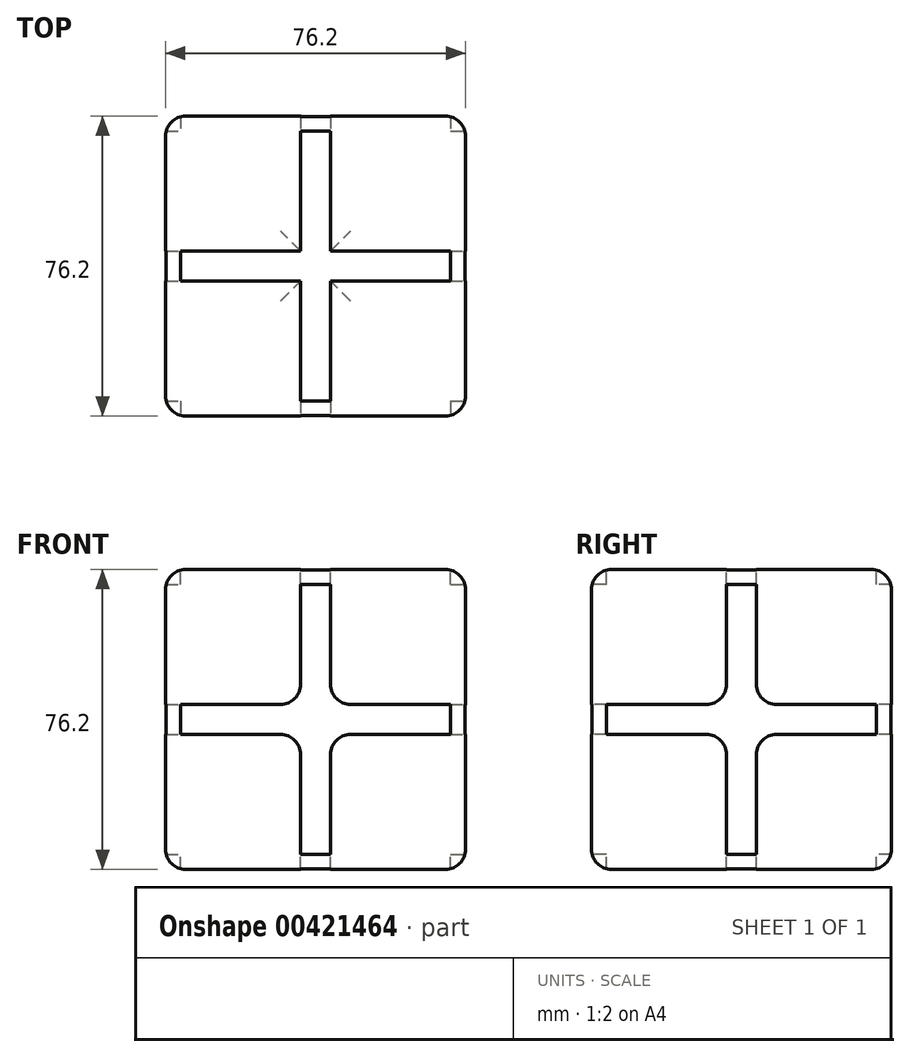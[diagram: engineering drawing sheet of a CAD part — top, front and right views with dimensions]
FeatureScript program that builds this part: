
annotation { "Feature Type Name" : "Feature", "Feature Type Description" : "" }
export const myFeature = defineFeature(function(context is Context, id is Id, definition is map)
    precondition{}
    {
        {
            var Q0;
            Q0=qCreatedBy(makeId("Top.planeOp"),FACE);
            var sketch = newSketch(context, id + "F0", { "sketchPlane" : qUnion([Q0])});
            skLineSegment(sketch, "E0.bottom", {"start": v(-38.1, 38.1) * mm, "end": v(38.1, 38.1) * mm});
            skLineSegment(sketch, "E0.top", {"start": v(-38.1, -38.1) * mm, "end": v(38.1, -38.1) * mm});
            skLineSegment(sketch, "E0.left", {"start": v(-38.1, 38.1) * mm, "end": v(-38.1, -38.1) * mm});
            skLineSegment(sketch, "E0.right", {"start": v(38.1, 38.1) * mm, "end": v(38.1, -38.1) * mm});
            skSolve(sketch);
        }
        {
            var Q0;
            Q0=makeQuery(id+"F0.imprint","IMPRINT",FACE,{"disambiguationData":[TD([[makeQuery(id+"F0.imprint","IMPRINT",EDGE,{"derivedFrom":sQuery(id+"F0.wireOp",EDGE,"E0.bottom")}),-1.0]])]});
            extrude(context, id + "F1", {"entities" : qUnion([Q0]), "depth" : 76.2 * mm});
        }
        {
            var Q0;
            Q0=makeQuery(id+"F1.opExtrude","SWEPT_FACE",FACE,{"disambiguationData":[OSD([sQuery(id+"F0.wireOp",EDGE,"E0.top")])]});
            var sketch = newSketch(context, id + "F2", { "sketchPlane" : qUnion([Q0])});
            skLineSegment(sketch, "E1", {"start": v(-34.3, 41.91) * mm, "end": v(-3.81, 41.91) * mm});
            skLineSegment(sketch, "E2", {"start": v(-34.3, 34.3) * mm, "end": v(-3.81, 34.3) * mm});
            skLineSegment(sketch, "E3", {"start": v(-3.81, 41.91) * mm, "end": v(-3.81, 72.39) * mm});
            skLineSegment(sketch, "E4", {"start": v(-3.81, 34.3) * mm, "end": v(-3.81, 3.8) * mm});
            skLineSegment(sketch, "E5", {"start": v(34.3, 41.91) * mm, "end": v(3.8, 41.91) * mm});
            skLineSegment(sketch, "E6", {"start": v(34.3, 34.3) * mm, "end": v(3.8, 34.3) * mm});
            skLineSegment(sketch, "E7", {"start": v(3.8, 41.91) * mm, "end": v(3.8, 72.39) * mm});
            skLineSegment(sketch, "E8", {"start": v(3.8, 34.3) * mm, "end": v(3.8, 3.81) * mm});
            skLineSegment(sketch, "E9", {"start": v(-34.3, 41.9) * mm, "end": v(-34.3, 34.3) * mm});
            skLineSegment(sketch, "E10.MirrorCS", {"start": v(34.3, 41.9) * mm, "end": v(34.3, 34.3) * mm});
            skPoint(sketch, "E11.right.end.orphan", {"position": v(38.1, 34.3) * mm});
            skPoint(sketch, "E11.right.start.orphan", {"position": v(38.1, 41.91) * mm});
            skLineSegment(sketch, "E12", {"start": v(-3.81, 3.8) * mm, "end": v(3.8, 3.8) * mm});
            skLineSegment(sketch, "E13.MirrorCS", {"start": v(-3.81, 72.39) * mm, "end": v(3.8, 72.39) * mm});
            skPoint(sketch, "E14.end.orphan", {"position": v(34.3, 38.1) * mm});
            skPoint(sketch, "E14.start.orphan", {"position": v(-34.3, 38.1) * mm});
            skSolve(sketch);
        }
        {
            var Q0;
            Q0=makeQuery(id+"F2.imprint","IMPRINT",FACE,{"disambiguationData":[TD([[makeQuery(id+"F2.imprint","IMPRINT",EDGE,{"derivedFrom":sQuery(id+"F2.wireOp",EDGE,"E1")}),-1.0]])]});
            extrude(context, id + "F3", {"entities" : qUnion([Q0]), "operationType" : NewBodyOperationType.REMOVE, "oppositeDirection" : true, "depth" : 76.2 * mm});
        }
        {
            var Q0;
            Q0=makeQuery(id+"F1.opExtrude","CAP_FACE",FACE,{"disambiguationData":[OSD([sQuery(id+"F0.wireOp",EDGE,"E0.bottom"),sQuery(id+"F0.wireOp",EDGE,"E0.top"),sQuery(id+"F0.wireOp",EDGE,"E0.left"),sQuery(id+"F0.wireOp",EDGE,"E0.right")])],"isStart":false});
            var sketch = newSketch(context, id + "F4", { "sketchPlane" : qUnion([Q0])});
            skLineSegment(sketch, "E15", {"start": v(-3.81, 34.3) * mm, "end": v(-3.81, 3.8) * mm});
            skPoint(sketch, "E15.endSnap0", {"position": v(0, -38.1) * mm});
            skLineSegment(sketch, "E16", {"start": v(3.8, -34.29) * mm, "end": v(3.8, -3.8) * mm});
            skLineSegment(sketch, "E17", {"start": v(-34.3, 3.8) * mm, "end": v(-3.81, 3.8) * mm});
            skLineSegment(sketch, "E18", {"start": v(34.29, -3.8) * mm, "end": v(3.8, -3.8) * mm});
            skLineSegment(sketch, "E19.trimOffspring", {"start": v(3.8, 3.8) * mm, "end": v(34.29, 3.8) * mm});
            skLineSegment(sketch, "E20.trimOffspring", {"start": v(-3.81, -3.81) * mm, "end": v(-3.81, -34.29) * mm});
            skLineSegment(sketch, "E21.trimOffspring", {"start": v(3.8, 3.8) * mm, "end": v(3.8, 34.3) * mm});
            skLineSegment(sketch, "E22.trimOffspring", {"start": v(-3.81, -3.8) * mm, "end": v(-34.3, -3.81) * mm});
            skLineSegment(sketch, "E23", {"start": v(-34.3, 3.8) * mm, "end": v(-34.3, -3.81) * mm});
            skLineSegment(sketch, "E24", {"start": v(34.29, 3.8) * mm, "end": v(34.29, -3.8) * mm});
            skLineSegment(sketch, "E25", {"start": v(-3.81, 34.3) * mm, "end": v(3.8, 34.3) * mm});
            skLineSegment(sketch, "E26", {"start": v(-3.81, -34.29) * mm, "end": v(3.8, -34.29) * mm});
            skPoint(sketch, "E27.start.orphan", {"position": v(-3.81, -38.1) * mm});
            skSolve(sketch);
        }
        {
            var Q0;
            Q0=makeQuery(id+"F4.imprint","IMPRINT",FACE,{"disambiguationData":[TD([[makeQuery(id+"F4.imprint","IMPRINT",EDGE,{"derivedFrom":sQuery(id+"F4.wireOp",EDGE,"E15")}),1.0]])]});
            extrude(context, id + "F5", {"entities" : qUnion([Q0]), "operationType" : NewBodyOperationType.REMOVE, "oppositeDirection" : true, "depth" : 76.2 * mm});
        }
        {
            var Q0;
            Q0=makeQuery(id+"F1.opExtrude","SWEPT_FACE",FACE,{"disambiguationData":[OSD([sQuery(id+"F0.wireOp",EDGE,"E0.right")])]});
            var sketch = newSketch(context, id + "F6", { "sketchPlane" : qUnion([Q0])});
            skLineSegment(sketch, "E28", {"start": v(-34.3, 41.9) * mm, "end": v(-3.8, 41.9) * mm});
            skLineSegment(sketch, "E29", {"start": v(34.29, 34.3) * mm, "end": v(3.8, 34.3) * mm});
            skLineSegment(sketch, "E30", {"start": v(-3.8, 72.4) * mm, "end": v(-3.8, 41.9) * mm});
            skLineSegment(sketch, "E31", {"start": v(3.8, 3.81) * mm, "end": v(3.8, 34.3) * mm});
            skLineSegment(sketch, "E32", {"start": v(3.8, 72.4) * mm, "end": v(-3.8, 72.4) * mm});
            skLineSegment(sketch, "E33.trimOffspring", {"start": v(-3.8, 34.3) * mm, "end": v(-3.8, 3.81) * mm});
            skLineSegment(sketch, "E34.trimOffspring", {"start": v(3.8, 41.9) * mm, "end": v(34.29, 41.91) * mm});
            skLineSegment(sketch, "E35.trimOffspring", {"start": v(3.8, 41.9) * mm, "end": v(3.8, 72.4) * mm});
            skLineSegment(sketch, "E36.trimOffspring", {"start": v(-3.8, 34.3) * mm, "end": v(-34.3, 34.3) * mm});
            skLineSegment(sketch, "E37", {"start": v(-3.8, 3.81) * mm, "end": v(3.8, 3.81) * mm});
            skLineSegment(sketch, "E38", {"start": v(-34.3, 41.9) * mm, "end": v(-34.3, 34.3) * mm});
            skPoint(sketch, "E39.end.orphan", {"position": v(-41.91, 41.9) * mm});
            skPoint(sketch, "E40.orphan", {"position": v(-41.91, 34.3) * mm});
            skLineSegment(sketch, "E41.MirrorCS", {"start": v(34.29, 41.9) * mm, "end": v(34.29, 34.3) * mm});
            skSolve(sketch);
        }
        {
            var Q0;
            Q0=makeQuery(id+"F6.imprint","IMPRINT",FACE,{"disambiguationData":[TD([[makeQuery(id+"F6.imprint","IMPRINT",EDGE,{"derivedFrom":sQuery(id+"F6.wireOp",EDGE,"E28")}),-1.0]])]});
            extrude(context, id + "F7", {"entities" : qUnion([Q0]), "operationType" : NewBodyOperationType.REMOVE, "oppositeDirection" : true, "depth" : 76.2 * mm});
        }
        {
            var Q0;
            Q0=makeQuery(id+"F1.opExtrude","SWEPT_EDGE",EDGE,{"disambiguationData":[OSD([sQuery(id+"F0.wireOp",EDGE,"E0.top"),sQuery(id+"F0.wireOp",EDGE,"E0.right")])]});
            var Q1;
            Q1=makeQuery(id+"F1.opExtrude","CAP_EDGE",EDGE,{"disambiguationData":[OSD([sQuery(id+"F0.wireOp",EDGE,"E0.top")])],"isStart":false});
            var Q2;
            Q2=makeQuery(id+"F1.opExtrude","CAP_EDGE",EDGE,{"disambiguationData":[OSD([sQuery(id+"F0.wireOp",EDGE,"E0.right")])],"isStart":false});
            var Q3;
            Q3=makeQuery(id+"F1.opExtrude","SWEPT_EDGE",EDGE,{"disambiguationData":[OSD([sQuery(id+"F0.wireOp",EDGE,"E0.top"),sQuery(id+"F0.wireOp",EDGE,"E0.left")])]});
            var Q4;
            Q4=makeQuery(id+"F1.opExtrude","CAP_EDGE",EDGE,{"disambiguationData":[OSD([sQuery(id+"F0.wireOp",EDGE,"E0.top")])],"isStart":true});
            var Q5;
            Q5=makeQuery(id+"F1.opExtrude","CAP_EDGE",EDGE,{"disambiguationData":[OSD([sQuery(id+"F0.wireOp",EDGE,"E0.right")])],"isStart":true});
            var Q6;
            Q6=makeQuery(id+"F1.opExtrude","SWEPT_EDGE",EDGE,{"disambiguationData":[OSD([sQuery(id+"F0.wireOp",EDGE,"E0.bottom"),sQuery(id+"F0.wireOp",EDGE,"E0.right")])]});
            var Q7;
            Q7=makeQuery(id+"F1.opExtrude","CAP_EDGE",EDGE,{"disambiguationData":[OSD([sQuery(id+"F0.wireOp",EDGE,"E0.bottom")])],"isStart":false});
            var Q8;
            Q8=makeQuery(id+"F1.opExtrude","CAP_EDGE",EDGE,{"disambiguationData":[OSD([sQuery(id+"F0.wireOp",EDGE,"E0.left")])],"isStart":false});
            var Q9;
            Q9=makeQuery(id+"F1.opExtrude","SWEPT_EDGE",EDGE,{"disambiguationData":[OSD([sQuery(id+"F0.wireOp",EDGE,"E0.bottom"),sQuery(id+"F0.wireOp",EDGE,"E0.left")])]});
            var Q10;
            Q10=makeQuery(id+"F1.opExtrude","CAP_EDGE",EDGE,{"disambiguationData":[OSD([sQuery(id+"F0.wireOp",EDGE,"E0.left")])],"isStart":true});
            var Q11;
            Q11=makeQuery(id+"F1.opExtrude","CAP_EDGE",EDGE,{"disambiguationData":[OSD([sQuery(id+"F0.wireOp",EDGE,"E0.bottom")])],"isStart":true});
            fillet(context, id + "F8", {"entities" : qUnion([Q0, Q1, Q2, Q3, Q4, Q5, Q6, Q7, Q8, Q9, Q10, Q11]), "radius" : 5.08 * mm, "tangentPropagation" : true, "allowEdgeOverflow" : false});
        }
        {
            var Q0;
            {var subQ0=sQuery(id+"F2.wireOp",EDGE,"E6");var subQ1=sQuery(id+"F2.wireOp",EDGE,"E8");Q0=makeQuery(id+"F5.boolean.opBoolean","SPLIT",EDGE,{"disambiguationData":[topologyDisambiguationEdgeConnected([makeQuery(id+"F5.opExtrude","SWEPT_FACE",FACE,{"disambiguationData":[OSD([sQuery(id+"F4.wireOp",EDGE,"E21.trimOffspring")])]})])],"derivedFrom":makeQuery(id+"F3.boolean.opBoolean","COPY",EDGE,{"derivedFrom":makeQuery(id+"F3.opExtrude","SWEPT_EDGE",EDGE,{"disambiguationData":[OSD([subQ0,subQ1])]})})});}
            var Q1;
            {var subQ0=sQuery(id+"F2.wireOp",EDGE,"E5");var subQ1=sQuery(id+"F2.wireOp",EDGE,"E7");Q1=makeQuery(id+"F5.boolean.opBoolean","SPLIT",EDGE,{"disambiguationData":[topologyDisambiguationEdgeConnected([makeQuery(id+"F5.opExtrude","SWEPT_FACE",FACE,{"disambiguationData":[OSD([sQuery(id+"F4.wireOp",EDGE,"E21.trimOffspring")])]})])],"derivedFrom":makeQuery(id+"F3.boolean.opBoolean","COPY",EDGE,{"derivedFrom":makeQuery(id+"F3.opExtrude","SWEPT_EDGE",EDGE,{"disambiguationData":[OSD([subQ0,subQ1])]})})});}
            var Q2;
            {var subQ0=sQuery(id+"F2.wireOp",EDGE,"E2");var subQ1=sQuery(id+"F2.wireOp",EDGE,"E4");Q2=makeQuery(id+"F5.boolean.opBoolean","SPLIT",EDGE,{"disambiguationData":[topologyDisambiguationEdgeConnected([makeQuery(id+"F5.opExtrude","SWEPT_FACE",FACE,{"disambiguationData":[OSD([sQuery(id+"F4.wireOp",EDGE,"E15")])]})])],"derivedFrom":makeQuery(id+"F3.boolean.opBoolean","COPY",EDGE,{"derivedFrom":makeQuery(id+"F3.opExtrude","SWEPT_EDGE",EDGE,{"disambiguationData":[OSD([subQ0,subQ1])]})})});}
            var Q3;
            {var subQ0=sQuery(id+"F2.wireOp",EDGE,"E1");var subQ1=sQuery(id+"F2.wireOp",EDGE,"E3");Q3=makeQuery(id+"F5.boolean.opBoolean","SPLIT",EDGE,{"disambiguationData":[topologyDisambiguationEdgeConnected([makeQuery(id+"F5.opExtrude","SWEPT_FACE",FACE,{"disambiguationData":[OSD([sQuery(id+"F4.wireOp",EDGE,"E15")])]})])],"derivedFrom":makeQuery(id+"F3.boolean.opBoolean","COPY",EDGE,{"derivedFrom":makeQuery(id+"F3.opExtrude","SWEPT_EDGE",EDGE,{"disambiguationData":[OSD([subQ0,subQ1])]})})});}
            var Q4;
            Q4=makeQuery(id+"F7.boolean.opBoolean","MERGE",EDGE,{"derivedFrom":[makeQuery(id+"F5.boolean.opBoolean","INTERSECT",EDGE,{"derivedFrom":[makeQuery(id+"F3.boolean.opBoolean","COPY",FACE,{"derivedFrom":makeQuery(id+"F3.opExtrude","SWEPT_FACE",FACE,{"disambiguationData":[OSD([sQuery(id+"F2.wireOp",EDGE,"E6")])]})}),makeQuery(id+"F5.opExtrude","SWEPT_FACE",FACE,{"disambiguationData":[OSD([sQuery(id+"F4.wireOp",EDGE,"E19.trimOffspring")])]})]}),makeQuery(id+"F7.opExtrude","SWEPT_EDGE",EDGE,{"disambiguationData":[OSD([sQuery(id+"F6.wireOp",EDGE,"E29"),sQuery(id+"F6.wireOp",EDGE,"E31")])]})]});
            var Q5;
            Q5=makeQuery(id+"F7.boolean.opBoolean","MERGE",EDGE,{"derivedFrom":[makeQuery(id+"F5.boolean.opBoolean","INTERSECT",EDGE,{"derivedFrom":[makeQuery(id+"F3.boolean.opBoolean","COPY",FACE,{"derivedFrom":makeQuery(id+"F3.opExtrude","SWEPT_FACE",FACE,{"disambiguationData":[OSD([sQuery(id+"F2.wireOp",EDGE,"E6")])]})}),makeQuery(id+"F5.opExtrude","SWEPT_FACE",FACE,{"disambiguationData":[OSD([sQuery(id+"F4.wireOp",EDGE,"E18")])]})]}),makeQuery(id+"F7.opExtrude","SWEPT_EDGE",EDGE,{"disambiguationData":[OSD([sQuery(id+"F6.wireOp",EDGE,"E33.trimOffspring"),sQuery(id+"F6.wireOp",EDGE,"E36.trimOffspring")])]})]});
            var Q6;
            Q6=makeQuery(id+"F7.boolean.opBoolean","MERGE",EDGE,{"derivedFrom":[makeQuery(id+"F5.boolean.opBoolean","INTERSECT",EDGE,{"derivedFrom":[makeQuery(id+"F3.boolean.opBoolean","COPY",FACE,{"derivedFrom":makeQuery(id+"F3.opExtrude","SWEPT_FACE",FACE,{"disambiguationData":[OSD([sQuery(id+"F2.wireOp",EDGE,"E5")])]})}),makeQuery(id+"F5.opExtrude","SWEPT_FACE",FACE,{"disambiguationData":[OSD([sQuery(id+"F4.wireOp",EDGE,"E18")])]})]}),makeQuery(id+"F7.opExtrude","SWEPT_EDGE",EDGE,{"disambiguationData":[OSD([sQuery(id+"F6.wireOp",EDGE,"E28"),sQuery(id+"F6.wireOp",EDGE,"E30")])]})]});
            var Q7;
            Q7=makeQuery(id+"F7.boolean.opBoolean","MERGE",EDGE,{"derivedFrom":[makeQuery(id+"F5.boolean.opBoolean","INTERSECT",EDGE,{"derivedFrom":[makeQuery(id+"F3.boolean.opBoolean","COPY",FACE,{"derivedFrom":makeQuery(id+"F3.opExtrude","SWEPT_FACE",FACE,{"disambiguationData":[OSD([sQuery(id+"F2.wireOp",EDGE,"E5")])]})}),makeQuery(id+"F5.opExtrude","SWEPT_FACE",FACE,{"disambiguationData":[OSD([sQuery(id+"F4.wireOp",EDGE,"E19.trimOffspring")])]})]}),makeQuery(id+"F7.opExtrude","SWEPT_EDGE",EDGE,{"disambiguationData":[OSD([sQuery(id+"F6.wireOp",EDGE,"E34.trimOffspring"),sQuery(id+"F6.wireOp",EDGE,"E35.trimOffspring")])]})]});
            var Q8;
            {var subQ0=sQuery(id+"F2.wireOp",EDGE,"E2");var subQ1=sQuery(id+"F2.wireOp",EDGE,"E4");Q8=makeQuery(id+"F5.boolean.opBoolean","SPLIT",EDGE,{"disambiguationData":[topologyDisambiguationEdgeConnected([makeQuery(id+"F5.opExtrude","SWEPT_FACE",FACE,{"disambiguationData":[OSD([sQuery(id+"F4.wireOp",EDGE,"E20.trimOffspring")])]})])],"derivedFrom":makeQuery(id+"F3.boolean.opBoolean","COPY",EDGE,{"derivedFrom":makeQuery(id+"F3.opExtrude","SWEPT_EDGE",EDGE,{"disambiguationData":[OSD([subQ0,subQ1])]})})});}
            var Q9;
            {var subQ0=sQuery(id+"F2.wireOp",EDGE,"E1");var subQ1=sQuery(id+"F2.wireOp",EDGE,"E3");Q9=makeQuery(id+"F5.boolean.opBoolean","SPLIT",EDGE,{"disambiguationData":[topologyDisambiguationEdgeConnected([makeQuery(id+"F5.opExtrude","SWEPT_FACE",FACE,{"disambiguationData":[OSD([sQuery(id+"F4.wireOp",EDGE,"E20.trimOffspring")])]})])],"derivedFrom":makeQuery(id+"F3.boolean.opBoolean","COPY",EDGE,{"derivedFrom":makeQuery(id+"F3.opExtrude","SWEPT_EDGE",EDGE,{"disambiguationData":[OSD([subQ0,subQ1])]})})});}
            var Q10;
            {var subQ0=sQuery(id+"F2.wireOp",EDGE,"E6");var subQ1=sQuery(id+"F2.wireOp",EDGE,"E8");Q10=makeQuery(id+"F5.boolean.opBoolean","SPLIT",EDGE,{"disambiguationData":[topologyDisambiguationEdgeConnected([makeQuery(id+"F5.opExtrude","SWEPT_FACE",FACE,{"disambiguationData":[OSD([sQuery(id+"F4.wireOp",EDGE,"E16")])]})])],"derivedFrom":makeQuery(id+"F3.boolean.opBoolean","COPY",EDGE,{"derivedFrom":makeQuery(id+"F3.opExtrude","SWEPT_EDGE",EDGE,{"disambiguationData":[OSD([subQ0,subQ1])]})})});}
            var Q11;
            {var subQ0=sQuery(id+"F2.wireOp",EDGE,"E5");var subQ1=sQuery(id+"F2.wireOp",EDGE,"E7");Q11=makeQuery(id+"F5.boolean.opBoolean","SPLIT",EDGE,{"disambiguationData":[topologyDisambiguationEdgeConnected([makeQuery(id+"F5.opExtrude","SWEPT_FACE",FACE,{"disambiguationData":[OSD([sQuery(id+"F4.wireOp",EDGE,"E16")])]})])],"derivedFrom":makeQuery(id+"F3.boolean.opBoolean","COPY",EDGE,{"derivedFrom":makeQuery(id+"F3.opExtrude","SWEPT_EDGE",EDGE,{"disambiguationData":[OSD([subQ0,subQ1])]})})});}
            var Q12;
            Q12=makeQuery(id+"F7.boolean.opBoolean","MERGE",EDGE,{"derivedFrom":[makeQuery(id+"F5.boolean.opBoolean","INTERSECT",EDGE,{"derivedFrom":[makeQuery(id+"F3.boolean.opBoolean","COPY",FACE,{"derivedFrom":makeQuery(id+"F3.opExtrude","SWEPT_FACE",FACE,{"disambiguationData":[OSD([sQuery(id+"F2.wireOp",EDGE,"E1")])]})}),makeQuery(id+"F5.opExtrude","SWEPT_FACE",FACE,{"disambiguationData":[OSD([sQuery(id+"F4.wireOp",EDGE,"E17")])]})]}),makeQuery(id+"F7.opExtrude","SWEPT_EDGE",EDGE,{"disambiguationData":[OSD([sQuery(id+"F6.wireOp",EDGE,"E34.trimOffspring"),sQuery(id+"F6.wireOp",EDGE,"E35.trimOffspring")])]})]});
            var Q13;
            Q13=makeQuery(id+"F7.boolean.opBoolean","MERGE",EDGE,{"derivedFrom":[makeQuery(id+"F5.boolean.opBoolean","INTERSECT",EDGE,{"derivedFrom":[makeQuery(id+"F3.boolean.opBoolean","COPY",FACE,{"derivedFrom":makeQuery(id+"F3.opExtrude","SWEPT_FACE",FACE,{"disambiguationData":[OSD([sQuery(id+"F2.wireOp",EDGE,"E2")])]})}),makeQuery(id+"F5.opExtrude","SWEPT_FACE",FACE,{"disambiguationData":[OSD([sQuery(id+"F4.wireOp",EDGE,"E17")])]})]}),makeQuery(id+"F7.opExtrude","SWEPT_EDGE",EDGE,{"disambiguationData":[OSD([sQuery(id+"F6.wireOp",EDGE,"E29"),sQuery(id+"F6.wireOp",EDGE,"E31")])]})]});
            var Q14;
            Q14=makeQuery(id+"F7.boolean.opBoolean","MERGE",EDGE,{"derivedFrom":[makeQuery(id+"F5.boolean.opBoolean","INTERSECT",EDGE,{"derivedFrom":[makeQuery(id+"F3.boolean.opBoolean","COPY",FACE,{"derivedFrom":makeQuery(id+"F3.opExtrude","SWEPT_FACE",FACE,{"disambiguationData":[OSD([sQuery(id+"F2.wireOp",EDGE,"E2")])]})}),makeQuery(id+"F5.opExtrude","SWEPT_FACE",FACE,{"disambiguationData":[OSD([sQuery(id+"F4.wireOp",EDGE,"E22.trimOffspring")])]})]}),makeQuery(id+"F7.opExtrude","SWEPT_EDGE",EDGE,{"disambiguationData":[OSD([sQuery(id+"F6.wireOp",EDGE,"E33.trimOffspring"),sQuery(id+"F6.wireOp",EDGE,"E36.trimOffspring")])]})]});
            var Q15;
            Q15=makeQuery(id+"F7.boolean.opBoolean","MERGE",EDGE,{"derivedFrom":[makeQuery(id+"F5.boolean.opBoolean","INTERSECT",EDGE,{"derivedFrom":[makeQuery(id+"F3.boolean.opBoolean","COPY",FACE,{"derivedFrom":makeQuery(id+"F3.opExtrude","SWEPT_FACE",FACE,{"disambiguationData":[OSD([sQuery(id+"F2.wireOp",EDGE,"E1")])]})}),makeQuery(id+"F5.opExtrude","SWEPT_FACE",FACE,{"disambiguationData":[OSD([sQuery(id+"F4.wireOp",EDGE,"E22.trimOffspring")])]})]}),makeQuery(id+"F7.opExtrude","SWEPT_EDGE",EDGE,{"disambiguationData":[OSD([sQuery(id+"F6.wireOp",EDGE,"E28"),sQuery(id+"F6.wireOp",EDGE,"E30")])]})]});
            fillet(context, id + "F9", {"entities" : qUnion([Q0, Q1, Q2, Q3, Q4, Q5, Q6, Q7, Q8, Q9, Q10, Q11, Q12, Q13, Q14, Q15]), "radius" : 5.08 * mm, "tangentPropagation" : true, "allowEdgeOverflow" : false});
        }
    });
